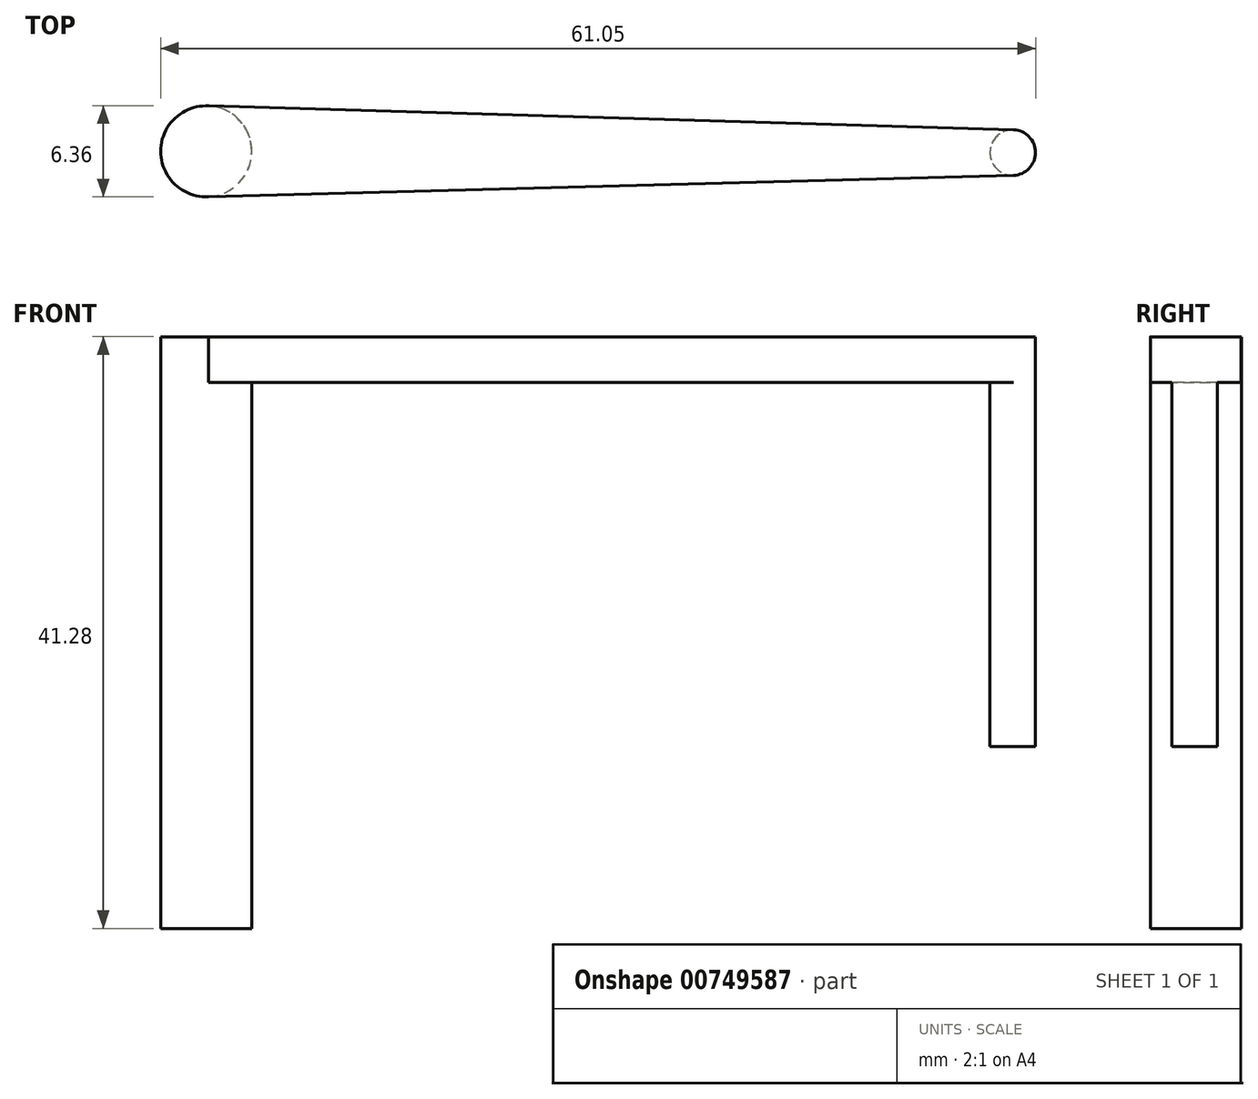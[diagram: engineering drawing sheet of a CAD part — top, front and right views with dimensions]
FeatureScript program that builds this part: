
annotation { "Feature Type Name" : "Feature", "Feature Type Description" : "" }
export const myFeature = defineFeature(function(context is Context, id is Id, definition is map)
    precondition{}
    {
        {
            var Q0;
            Q0=qCreatedBy(makeId("Top.planeOp"),FACE);
            var sketch = newSketch(context, id + "F0", { "sketchPlane" : qUnion([Q0])});
            skCircle(sketch, "E0", {"center": v(0, 0) * mm, "radius": 3.18 * mm});
            skSolve(sketch);
        }
        {
            var Q0;
            Q0 = qSketchRegion(id + "F0", true);
            extrude(context, id + "F1", {"entities" : qUnion([Q0]), "depth" : 38.1 * mm, "offsetDistance" : 25.4 * mm});
        }
        {
            var Q0;
            Q0=makeQuery(id+"F1.opExtrude","CAP_FACE",FACE,{"disambiguationData":[OSD([sQuery(id+"F0.wireOp",EDGE,"E0")])],"isStart":false});
            var sketch = newSketch(context, id + "F2", { "sketchPlane" : qUnion([Q0])});
            skArc(sketch, "E1.0", {"start": v(0.19, 3.17) * mm, "mid": v(-3.17, 0) * mm, "end": v(0.17, -3.17) * mm});
            skArc(sketch, "E2", {"start": v(56.32, -1.67) * mm, "mid": v(57.87, -0.09) * mm, "end": v(56.33, 1.5) * mm});
            skLineSegment(sketch, "E3", {"start": v(0, -3.18) * mm, "end": v(56.32, -1.67) * mm});
            skLineSegment(sketch, "E4", {"start": v(0, 3.18) * mm, "end": v(56.33, 1.5) * mm});
            skSolve(sketch);
        }
        {
            var Q0;
            Q0 = qSketchRegion(id + "F2", true);
            extrude(context, id + "F3", {"entities" : qUnion([Q0]), "operationType" : NewBodyOperationType.ADD, "depth" : 3.17 * mm, "offsetDistance" : 25.4 * mm});
        }
        {
            var Q0;
            Q0=makeQuery(id+"F3.opExtrude","CAP_FACE",FACE,{"disambiguationData":[OSD([sQuery(id+"F2.wireOp",EDGE,"E1.0"),sQuery(id+"F2.wireOp",EDGE,"E2"),sQuery(id+"F2.wireOp",EDGE,"E3"),sQuery(id+"F2.wireOp",EDGE,"E4")])],"isStart":true});
            var sketch = newSketch(context, id + "F4", { "sketchPlane" : qUnion([Q0])});
            skCircle(sketch, "E5", {"center": v(56.28, 0.09) * mm, "radius": 1.59 * mm});
            skPoint(sketch, "E5.first.point", {"position": v(57.87, 0.09) * mm});
            skPoint(sketch, "E5.first.point.positionSnap0", {"position": v(57.87, 0.09) * mm});
            skPoint(sketch, "E5.second.point", {"position": v(56.33, -1.5) * mm});
            skPoint(sketch, "E5.third.point", {"position": v(56.32, 1.67) * mm});
            skSolve(sketch);
        }
        {
            var Q0;
            Q0 = qSketchRegion(id + "F4", true);
            extrude(context, id + "F5", {"entities" : qUnion([Q0]), "operationType" : NewBodyOperationType.ADD, "depth" : 25.4 * mm, "offsetDistance" : 25.4 * mm});
        }
    });
